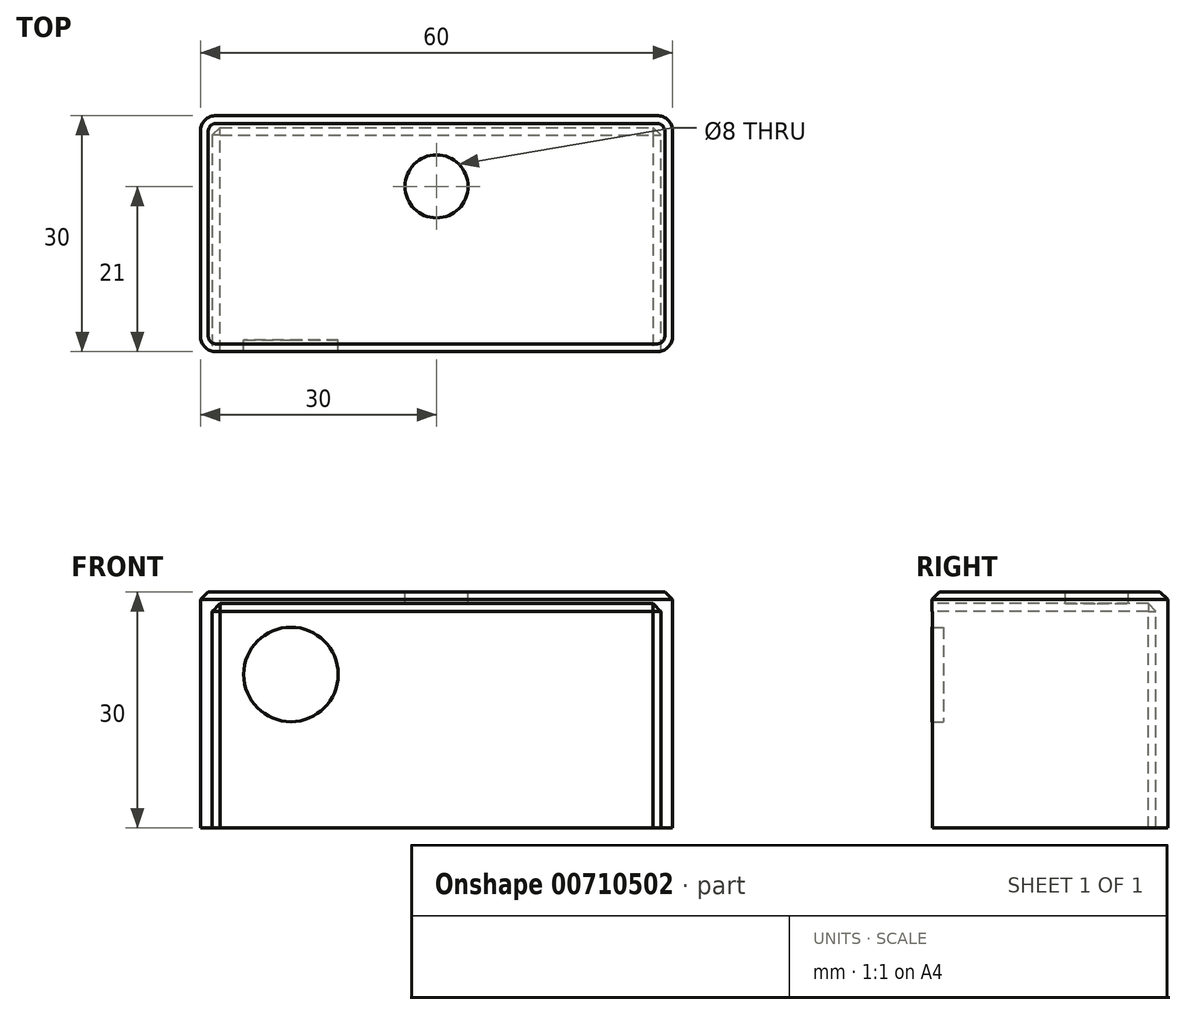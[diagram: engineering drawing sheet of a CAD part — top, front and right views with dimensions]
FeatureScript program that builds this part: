
annotation { "Feature Type Name" : "Feature", "Feature Type Description" : "" }
export const myFeature = defineFeature(function(context is Context, id is Id, definition is map)
    precondition{}
    {
        {
            var Q0;
            Q0=qCreatedBy(makeId("Top.planeOp"),FACE);
            var sketch = newSketch(context, id + "F0", { "sketchPlane" : qUnion([Q0])});
            skLineSegment(sketch, "E0.bottom", {"start": v(-30, 15) * mm, "end": v(30, 15) * mm});
            skLineSegment(sketch, "E0.top", {"start": v(-30, -15) * mm, "end": v(30, -15) * mm});
            skLineSegment(sketch, "E0.left", {"start": v(-30, 15) * mm, "end": v(-30, -15) * mm});
            skLineSegment(sketch, "E0.right", {"start": v(30, 15) * mm, "end": v(30, -15) * mm});
            skPoint(sketch, "E0.middle", {"position": v(0, 0) * mm});
            skSolve(sketch);
        }
        {
            var Q0;
            Q0=makeQuery(id+"F0.imprint","IMPRINT",FACE,{"disambiguationData":[TD([[makeQuery(id+"F0.imprint","IMPRINT",EDGE,{"derivedFrom":sQuery(id+"F0.wireOp",EDGE,"E0.bottom")}),-1.0]])]});
            extrude(context, id + "F1", {"entities" : qUnion([Q0]), "depth" : 30 * mm, "offsetDistance" : 25 * mm});
        }
        {
            var Q0;
            Q0=makeQuery(id+"F1.opExtrude","CAP_FACE",FACE,{"disambiguationData":[OSD([sQuery(id+"F0.wireOp",EDGE,"E0.bottom"),sQuery(id+"F0.wireOp",EDGE,"E0.top"),sQuery(id+"F0.wireOp",EDGE,"E0.left"),sQuery(id+"F0.wireOp",EDGE,"E0.right")])],"isStart":true});
            shell(context, id + "F2", {"entities" : qUnion([Q0]), "thickness" : 1.5 * mm});
        }
        {
            var Q0;
            Q0=makeQuery(id+"F2.opShell","OFFSET_FACE",FACE,{"disambiguationData":[OSD([sQuery(id+"F0.wireOp",EDGE,"E0.top")])]});
            var sketch = newSketch(context, id + "F3", { "sketchPlane" : qUnion([Q0])});
            skLineSegment(sketch, "E1", {"start": v(0, 0) * mm, "end": v(0, 28.5) * mm, "construction": true});
            skCircle(sketch, "E2", {"center": v(-18.5, 19.5) * mm, "radius": 6 * mm});
            skCircle(sketch, "E3.MirrorC", {"center": v(18.5, 19.5) * mm, "radius": 6 * mm});
            skSolve(sketch);
        }
        {
            var Q0;
            Q0=makeQuery(id+"F3.imprint","IMPRINT",FACE,{"disambiguationData":[TD([[makeQuery(id+"F3.imprint","IMPRINT",EDGE,{"derivedFrom":sQuery(id+"F3.wireOp",EDGE,"E2")}),1.0]])]});
            var Q1;
            Q1=makeQuery(id+"F3.imprint","IMPRINT",FACE,{"disambiguationData":[TD([[makeQuery(id+"F3.imprint","IMPRINT",EDGE,{"derivedFrom":sQuery(id+"F3.wireOp",EDGE,"E3.MirrorC")}),-1.0]])]});
            extrude(context, id + "F4", {"entities" : qUnion([Q0, Q1]), "operationType" : NewBodyOperationType.REMOVE, "endBound" : BoundingType.THROUGH_ALL, "oppositeDirection" : true, "depth" : 25 * mm, "offsetDistance" : 25 * mm});
        }
        {
            var Q0;
            Q0=makeQuery(id+"F1.opExtrude","CAP_FACE",FACE,{"disambiguationData":[OSD([sQuery(id+"F0.wireOp",EDGE,"E0.bottom"),sQuery(id+"F0.wireOp",EDGE,"E0.top"),sQuery(id+"F0.wireOp",EDGE,"E0.left"),sQuery(id+"F0.wireOp",EDGE,"E0.right")])],"isStart":false});
            var sketch = newSketch(context, id + "F5", { "sketchPlane" : qUnion([Q0])});
            skLineSegment(sketch, "E4", {"start": v(0, 15) * mm, "end": v(0, -15) * mm, "construction": true});
            skCircle(sketch, "E5", {"center": v(0, 6) * mm, "radius": 4 * mm});
            skSolve(sketch);
        }
        {
            var Q0;
            Q0=makeQuery(id+"F5.imprint","IMPRINT",FACE,{"disambiguationData":[TD([[makeQuery(id+"F5.imprint","IMPRINT",EDGE,{"derivedFrom":sQuery(id+"F5.wireOp",EDGE,"E5")}),1.0]])]});
            extrude(context, id + "F6", {"entities" : qUnion([Q0]), "operationType" : NewBodyOperationType.REMOVE, "endBound" : BoundingType.THROUGH_ALL, "oppositeDirection" : true, "depth" : 25 * mm, "offsetDistance" : 25 * mm});
        }
        {
            var Q0;
            Q0=makeQuery(id+"F1.opExtrude","SWEPT_EDGE",EDGE,{"disambiguationData":[OSD([sQuery(id+"F0.wireOp",EDGE,"E0.bottom"),sQuery(id+"F0.wireOp",EDGE,"E0.right")])]});
            var Q1;
            Q1=makeQuery(id+"F1.opExtrude","SWEPT_EDGE",EDGE,{"disambiguationData":[OSD([sQuery(id+"F0.wireOp",EDGE,"E0.top"),sQuery(id+"F0.wireOp",EDGE,"E0.right")])]});
            var Q2;
            Q2=makeQuery(id+"F1.opExtrude","SWEPT_EDGE",EDGE,{"disambiguationData":[OSD([sQuery(id+"F0.wireOp",EDGE,"E0.top"),sQuery(id+"F0.wireOp",EDGE,"E0.left")])]});
            var Q3;
            Q3=makeQuery(id+"F1.opExtrude","SWEPT_EDGE",EDGE,{"disambiguationData":[OSD([sQuery(id+"F0.wireOp",EDGE,"E0.bottom"),sQuery(id+"F0.wireOp",EDGE,"E0.left")])]});
            fillet(context, id + "F7", {"entities" : qUnion([Q0, Q1, Q2, Q3]), "radius" : 2 * mm, "tangentPropagation" : true, "allowEdgeOverflow" : false});
        }
        {
            var Q0;
            {var subQ0=sQuery(id+"F0.wireOp",EDGE,"E0.right");Q0=makeQuery(id+"F2.opShell","OFFSET_EDGE",EDGE,{"disambiguationData":[OSD([subQ0]),TDD([makeQuery(id+"F1.opExtrude","CAP_EDGE",EDGE,{"disambiguationData":[OSD([subQ0])],"isStart":false})])]});}
            var Q1;
            {var subQ0=sQuery(id+"F0.wireOp",EDGE,"E0.bottom");Q1=makeQuery(id+"F2.opShell","OFFSET_EDGE",EDGE,{"disambiguationData":[OSD([subQ0]),TDD([makeQuery(id+"F1.opExtrude","CAP_EDGE",EDGE,{"disambiguationData":[OSD([subQ0])],"isStart":false})])]});}
            var Q2;
            {var subQ0=sQuery(id+"F0.wireOp",EDGE,"E0.top");Q2=makeQuery(id+"F2.opShell","OFFSET_EDGE",EDGE,{"disambiguationData":[OSD([subQ0]),TDD([makeQuery(id+"F1.opExtrude","CAP_EDGE",EDGE,{"disambiguationData":[OSD([subQ0])],"isStart":false})])]});}
            var Q3;
            {var subQ0=sQuery(id+"F0.wireOp",EDGE,"E0.left");Q3=makeQuery(id+"F2.opShell","OFFSET_EDGE",EDGE,{"disambiguationData":[OSD([subQ0]),TDD([makeQuery(id+"F1.opExtrude","CAP_EDGE",EDGE,{"disambiguationData":[OSD([subQ0])],"isStart":false})])]});}
            var Q4;
            Q4=makeQuery(id+"F2.opShell","OFFSET_EDGE",EDGE,{"disambiguationData":[OSD([sQuery(id+"F0.wireOp",EDGE,"E0.top"),sQuery(id+"F0.wireOp",EDGE,"E0.right")])]});
            var Q5;
            Q5=makeQuery(id+"F2.opShell","OFFSET_EDGE",EDGE,{"disambiguationData":[OSD([sQuery(id+"F0.wireOp",EDGE,"E0.bottom"),sQuery(id+"F0.wireOp",EDGE,"E0.right")])]});
            var Q6;
            Q6=makeQuery(id+"F2.opShell","OFFSET_EDGE",EDGE,{"disambiguationData":[OSD([sQuery(id+"F0.wireOp",EDGE,"E0.top"),sQuery(id+"F0.wireOp",EDGE,"E0.left")])]});
            var Q7;
            Q7=makeQuery(id+"F2.opShell","OFFSET_EDGE",EDGE,{"disambiguationData":[OSD([sQuery(id+"F0.wireOp",EDGE,"E0.bottom"),sQuery(id+"F0.wireOp",EDGE,"E0.left")])]});
            var Q8;
            Q8=makeQuery(id+"F1.opExtrude","CAP_EDGE",EDGE,{"disambiguationData":[OSD([sQuery(id+"F0.wireOp",EDGE,"E0.bottom")])],"isStart":false});
            var Q9;
            Q9=makeQuery(id+"F1.opExtrude","CAP_EDGE",EDGE,{"disambiguationData":[OSD([sQuery(id+"F0.wireOp",EDGE,"E0.right")])],"isStart":false});
            var Q10;
            Q10=makeQuery(id+"F1.opExtrude","CAP_EDGE",EDGE,{"disambiguationData":[OSD([sQuery(id+"F0.wireOp",EDGE,"E0.left")])],"isStart":false});
            var Q11;
            Q11=makeQuery(id+"F1.opExtrude","CAP_EDGE",EDGE,{"disambiguationData":[OSD([sQuery(id+"F0.wireOp",EDGE,"E0.top")])],"isStart":false});
            chamfer(context, id + "F8", {"entities" : qUnion([Q0, Q1, Q2, Q3, Q4, Q5, Q6, Q7, Q8, Q9, Q10, Q11]), "width" : 1 * mm, "tangentPropagation" : true});
        }
    });
